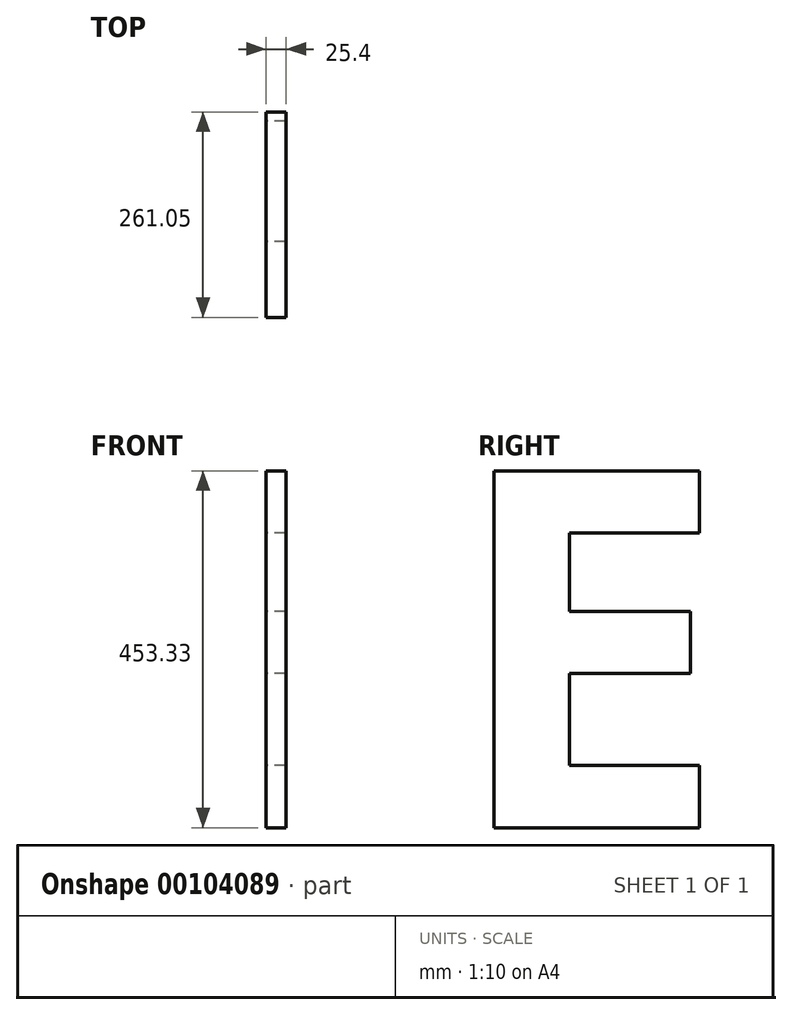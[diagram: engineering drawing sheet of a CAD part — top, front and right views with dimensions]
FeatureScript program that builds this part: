
annotation { "Feature Type Name" : "Feature", "Feature Type Description" : "" }
export const myFeature = defineFeature(function(context is Context, id is Id, definition is map)
    precondition{}
    {
        {
            var Q0;
            Q0=qCreatedBy(makeId("Right.planeOp"),FACE);
            var sketch = newSketch(context, id + "F0", { "sketchPlane" : qUnion([Q0])});
            skText(sketch, "E0", { "text": "E", "fontName": "OpenSans-Bold.ttf"});
            const initialGuessF0  = {"E0": [-0.3181, 0, 1, 0, 0.4572]};
            skSetInitialGuess(sketch, initialGuessF0);
            skSolve(sketch);
        }
        {
            var Q0;
            Q0 = qSketchRegion(id + "F0", true);
            extrude(context, id + "F1", {"entities" : qUnion([Q0]), "endBound" : BoundingType.SYMMETRIC, "depth" : 25.4 * mm});
        }
    });
